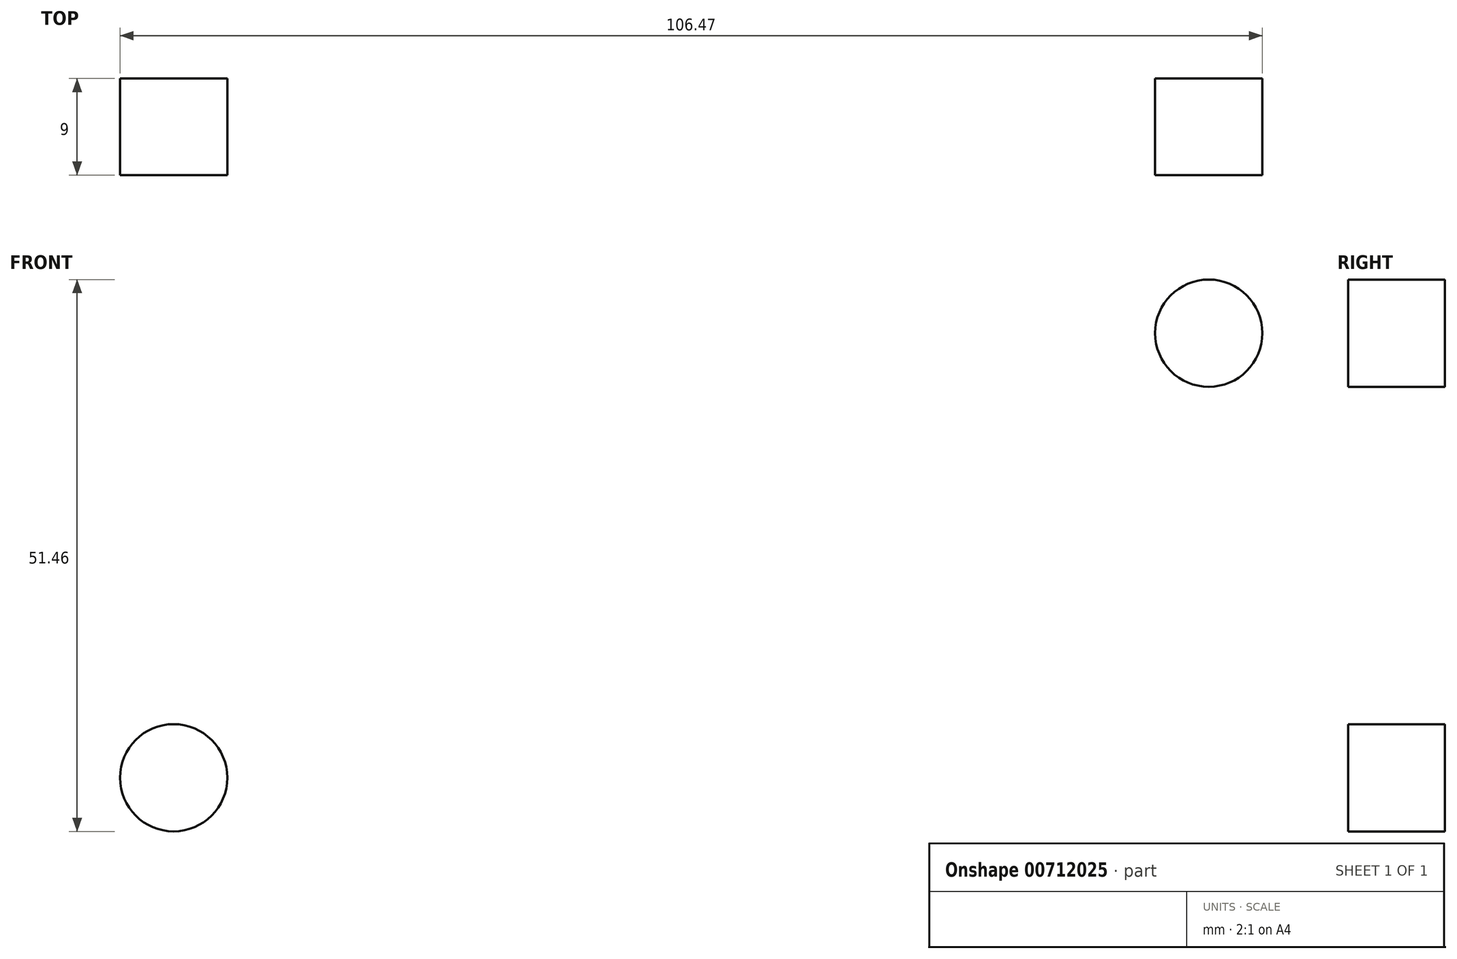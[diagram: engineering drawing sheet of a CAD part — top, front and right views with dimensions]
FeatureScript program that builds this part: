
annotation { "Feature Type Name" : "Feature", "Feature Type Description" : "" }
export const myFeature = defineFeature(function(context is Context, id is Id, definition is map)
    precondition{}
    {
        {
            var Q0;
            Q0=qCreatedBy(makeId("Front.planeOp"),FACE);
            var sketch = newSketch(context, id + "F0", { "sketchPlane" : qUnion([Q0])});
            skCircle(sketch, "E0", {"center": v(0, 0) * mm, "radius": 140 * mm});
            skArc(sketch, "E1", {"start": v(-19.84, 2.52) * mm, "mid": v(-17.32, -10) * mm, "end": v(-7.74, -18.44) * mm});
            skLineSegment(sketch, "E2", {"start": v(0, -20) * mm, "end": v(4.96, -19.38) * mm});
            skLineSegment(sketch, "E3", {"start": v(0, -20) * mm, "end": v(-4.96, -19.38) * mm});
            skArc(sketch, "E4", {"start": v(-6.37, -54.7) * mm, "mid": v(-4.56, -38.75) * mm, "end": v(-4.69, -22.7) * mm});
            skArc(sketch, "E5", {"start": v(4.69, -22.7) * mm, "mid": v(4.56, -38.75) * mm, "end": v(6.37, -54.7) * mm});
            skArc(sketch, "E6.1.0", {"start": v(50.55, 21.83) * mm, "mid": v(35.84, 15.43) * mm, "end": v(22, 7.3) * mm});
            skArc(sketch, "E6.1.1", {"start": v(17.32, 15.41) * mm, "mid": v(31.28, 23.32) * mm, "end": v(44.18, 32.86) * mm});
            skArc(sketch, "E6.2.0", {"start": v(-44.18, 32.86) * mm, "mid": v(-31.28, 23.32) * mm, "end": v(-17.32, 15.41) * mm});
            skArc(sketch, "E6.2.1", {"start": v(-22, 7.3) * mm, "mid": v(-35.84, 15.43) * mm, "end": v(-50.55, 21.83) * mm});
            skArc(sketch, "E7.trimOffspring", {"start": v(12.1, 15.93) * mm, "mid": v(0, 20) * mm, "end": v(-12.1, 15.93) * mm});
            skArc(sketch, "E8.trimOffspring", {"start": v(7.74, -18.44) * mm, "mid": v(17.32, -10) * mm, "end": v(19.84, 2.52) * mm});
            skPoint(sketch, "E9.visualSharp", {"position": v(-19.26, 5.4) * mm});
            skArc(sketch, "E9.filletArc", {"start": v(-19.84, 2.52) * mm, "mid": v(-20.25, 5.21) * mm, "end": v(-22, 7.3) * mm});
            skPoint(sketch, "E10.visualSharp", {"position": v(-14.3, 13.98) * mm});
            skArc(sketch, "E10.filletArc", {"start": v(-17.32, 15.41) * mm, "mid": v(-14.64, 14.93) * mm, "end": v(-12.1, 15.93) * mm});
            skPoint(sketch, "E11.visualSharp", {"position": v(14.3, 13.98) * mm});
            skArc(sketch, "E11.filletArc", {"start": v(12.1, 15.93) * mm, "mid": v(14.64, 14.93) * mm, "end": v(17.32, 15.41) * mm});
            skPoint(sketch, "E12.visualSharp", {"position": v(19.26, 5.4) * mm});
            skArc(sketch, "E12.filletArc", {"start": v(22, 7.3) * mm, "mid": v(20.25, 5.21) * mm, "end": v(19.84, 2.52) * mm});
            skPoint(sketch, "E13.visualSharp", {"position": v(4.96, -19.38) * mm});
            skArc(sketch, "E13.filletArc", {"start": v(7.74, -18.44) * mm, "mid": v(5.61, -20.14) * mm, "end": v(4.69, -22.7) * mm});
            skPoint(sketch, "E14.visualSharp", {"position": v(-4.96, -19.37) * mm});
            skArc(sketch, "E14.filletArc", {"start": v(-4.69, -22.7) * mm, "mid": v(-5.61, -20.14) * mm, "end": v(-7.74, -18.44) * mm});
            skCircle(sketch, "E15", {"center": v(0, 0) * mm, "radius": 3 * mm});
            skArc(sketch, "E16", {"start": v(44.7, 40.03) * mm, "mid": v(0, 60) * mm, "end": v(-44.7, 40.03) * mm});
            skArc(sketch, "E17.trimOffspring", {"start": v(-57.01, 18.7) * mm, "mid": v(-51.96, -30) * mm, "end": v(-12.32, -58.72) * mm});
            skArc(sketch, "E18.trimOffspring", {"start": v(12.32, -58.72) * mm, "mid": v(51.96, -30) * mm, "end": v(57.01, 18.7) * mm});
            skPoint(sketch, "E19.start.orphan", {"position": v(0, -52.5) * mm});
            skPoint(sketch, "E20.visualSharp", {"position": v(47.92, 36.1) * mm});
            skArc(sketch, "E20.filletArc", {"start": v(44.18, 32.86) * mm, "mid": v(45.96, 36.33) * mm, "end": v(44.7, 40.03) * mm});
            skPoint(sketch, "E21.visualSharp", {"position": v(55.23, 23.45) * mm});
            skArc(sketch, "E21.filletArc", {"start": v(57.01, 18.7) * mm, "mid": v(54.45, 21.64) * mm, "end": v(50.55, 21.83) * mm});
            skPoint(sketch, "E22.visualSharp", {"position": v(7.31, -59.55) * mm});
            skArc(sketch, "E22.filletArc", {"start": v(6.37, -54.7) * mm, "mid": v(8.49, -57.97) * mm, "end": v(12.32, -58.72) * mm});
            skPoint(sketch, "E23.visualSharp", {"position": v(-7.31, -59.55) * mm});
            skArc(sketch, "E23.filletArc", {"start": v(-12.32, -58.72) * mm, "mid": v(-8.49, -57.97) * mm, "end": v(-6.37, -54.7) * mm});
            skPoint(sketch, "E24.visualSharp", {"position": v(-55.23, 23.45) * mm});
            skArc(sketch, "E24.filletArc", {"start": v(-50.55, 21.83) * mm, "mid": v(-54.45, 21.64) * mm, "end": v(-57.01, 18.7) * mm});
            skPoint(sketch, "E25.visualSharp", {"position": v(-47.92, 36.1) * mm});
            skArc(sketch, "E25.filletArc", {"start": v(-44.7, 40.03) * mm, "mid": v(-45.96, 36.33) * mm, "end": v(-44.18, 32.86) * mm});
            skSolve(sketch);
        }
        {
            var Q0;
            Q0=makeQuery(id+"F0.imprint","IMPRINT",FACE,{"disambiguationData":[TD([[makeQuery(id+"F0.imprint","IMPRINT",EDGE,{"derivedFrom":sQuery(id+"F0.wireOp",EDGE,"E0")}),1.0]])]});
            extrude(context, id + "F1", {"entities" : qUnion([Q0]), "depth" : 9 * mm, "offsetDistance" : 25 * mm});
        }
        {
            var Q0;
            Q0=makeQuery(id+"F1.opExtrude","CAP_FACE",FACE,{"disambiguationData":[OSD([sQuery(id+"F0.wireOp",EDGE,"E0"),sQuery(id+"F0.wireOp",EDGE,"ZIODKena-zUbL-tIHl-ZjhE-ZrVelXlwY1Jm"),sQuery(id+"F0.wireOp",EDGE,"E1"),sQuery(id+"F0.wireOp",EDGE,"E4"),sQuery(id+"F0.wireOp",EDGE,"E5"),sQuery(id+"F0.wireOp",EDGE,"E6.1.0"),sQuery(id+"F0.wireOp",EDGE,"E6.1.1"),sQuery(id+"F0.wireOp",EDGE,"E6.2.0"),sQuery(id+"F0.wireOp",EDGE,"E6.2.1"),sQuery(id+"F0.wireOp",EDGE,"E7.trimOffspring"),sQuery(id+"F0.wireOp",EDGE,"76695641-9587-4a37-a800-fdab59d5437e.trimOffspring"),sQuery(id+"F0.wireOp",EDGE,"f6a8adc9-3116-4a73-b52b-f80456312e99.trimOffspring"),sQuery(id+"F0.wireOp",EDGE,"E8.trimOffspring"),sQuery(id+"F0.wireOp",EDGE,"148b025b-7aa4-4f89-82ff-914ac9d1939e.filletArc"),sQuery(id+"F0.wireOp",EDGE,"86ef975f-c508-4600-84ae-cfea6c1fc3ab.filletArc"),sQuery(id+"F0.wireOp",EDGE,"E9.filletArc"),sQuery(id+"F0.wireOp",EDGE,"E10.filletArc"),sQuery(id+"F0.wireOp",EDGE,"E11.filletArc"),sQuery(id+"F0.wireOp",EDGE,"f91f4047-f748-427d-8daf-de76601a4d34.filletArc"),sQuery(id+"F0.wireOp",EDGE,"E12.filletArc"),sQuery(id+"F0.wireOp",EDGE,"b79df10b-0bd3-4566-90f7-f9393d15810a.filletArc"),sQuery(id+"F0.wireOp",EDGE,"80464fdd-c0e1-48fa-a2d0-9debf860864b.filletArc"),sQuery(id+"F0.wireOp",EDGE,"4b7ce50a-a466-4e5d-bdfc-4ef1ba62d836.filletArc"),sQuery(id+"F0.wireOp",EDGE,"E13.filletArc"),sQuery(id+"F0.wireOp",EDGE,"E14.filletArc"),sQuery(id+"F0.wireOp",EDGE,"E15")])],"isStart":true});
            var sketch = newSketch(context, id + "F2", { "sketchPlane" : qUnion([Q0])});
            skCircle(sketch, "E26", {"center": v(0, 0) * mm, "radius": 105 * mm});
            skCircle(sketch, "E27", {"center": v(96.47, -41.46) * mm, "radius": 5 * mm});
            skCircle(sketch, "E28.1.0", {"center": v(84.14, 62.81) * mm, "radius": 5 * mm});
            skCircle(sketch, "E28.2.0", {"center": v(-12.33, 104.27) * mm, "radius": 5 * mm});
            skCircle(sketch, "E28.3.0", {"center": v(-96.47, 41.46) * mm, "radius": 5 * mm});
            skCircle(sketch, "E28.4.0", {"center": v(-84.14, -62.81) * mm, "radius": 5 * mm});
            skCircle(sketch, "E28.5.0", {"center": v(12.33, -104.27) * mm, "radius": 5 * mm});
            skSolve(sketch);
        }
        {
            var Q0;
            {var subQ0=sQuery(id+"F2.wireOp",EDGE,"E28.4.0");var subQ1=sQuery(id+"F2.wireOp",EDGE,"E26");var subQ2=makeQuery(id+"F2.imprint","INTERSECT",VERTEX,{"disambiguationData":[OD(0.0)],"derivedFrom":[subQ1,subQ0]});Q0=makeQuery(id+"F2.imprint","IMPRINT",FACE,{"disambiguationData":[TD([[makeQuery(id+"F2.imprint","IMPRINT",EDGE,{"disambiguationData":[TD([[subQ2,-1.0]])],"derivedFrom":subQ1}),-1.0]])]});}
            var Q1;
            {var subQ0=sQuery(id+"F2.wireOp",EDGE,"E28.4.0");var subQ1=sQuery(id+"F2.wireOp",EDGE,"E26");var subQ2=makeQuery(id+"F2.imprint","INTERSECT",VERTEX,{"disambiguationData":[OD(0.0)],"derivedFrom":[subQ1,subQ0]});Q1=makeQuery(id+"F2.imprint","IMPRINT",FACE,{"disambiguationData":[TD([[makeQuery(id+"F2.imprint","IMPRINT",EDGE,{"disambiguationData":[TD([[subQ2,-1.0]])],"derivedFrom":subQ1}),1.0]])]});}
            var Q2;
            {var subQ0=sQuery(id+"F2.wireOp",EDGE,"E28.3.0");var subQ1=sQuery(id+"F2.wireOp",EDGE,"E26");var subQ2=makeQuery(id+"F2.imprint","INTERSECT",VERTEX,{"disambiguationData":[OD(0.0)],"derivedFrom":[subQ1,subQ0]});Q2=makeQuery(id+"F2.imprint","IMPRINT",FACE,{"disambiguationData":[TD([[makeQuery(id+"F2.imprint","IMPRINT",EDGE,{"disambiguationData":[TD([[subQ2,-1.0]])],"derivedFrom":subQ1}),-1.0]])]});}
            var Q3;
            {var subQ0=sQuery(id+"F2.wireOp",EDGE,"E28.3.0");var subQ1=sQuery(id+"F2.wireOp",EDGE,"E26");var subQ2=makeQuery(id+"F2.imprint","INTERSECT",VERTEX,{"disambiguationData":[OD(0.0)],"derivedFrom":[subQ1,subQ0]});Q3=makeQuery(id+"F2.imprint","IMPRINT",FACE,{"disambiguationData":[TD([[makeQuery(id+"F2.imprint","IMPRINT",EDGE,{"disambiguationData":[TD([[subQ2,-1.0]])],"derivedFrom":subQ1}),1.0]])]});}
            var Q4;
            {var subQ0=sQuery(id+"F2.wireOp",EDGE,"E28.2.0");var subQ1=sQuery(id+"F2.wireOp",EDGE,"E26");var subQ2=makeQuery(id+"F2.imprint","INTERSECT",VERTEX,{"disambiguationData":[OD(0.0)],"derivedFrom":[subQ1,subQ0]});Q4=makeQuery(id+"F2.imprint","IMPRINT",FACE,{"disambiguationData":[TD([[makeQuery(id+"F2.imprint","IMPRINT",EDGE,{"disambiguationData":[TD([[subQ2,-1.0]])],"derivedFrom":subQ1}),-1.0]])]});}
            var Q5;
            {var subQ0=sQuery(id+"F2.wireOp",EDGE,"E28.2.0");var subQ1=sQuery(id+"F2.wireOp",EDGE,"E26");var subQ2=makeQuery(id+"F2.imprint","INTERSECT",VERTEX,{"disambiguationData":[OD(0.0)],"derivedFrom":[subQ1,subQ0]});Q5=makeQuery(id+"F2.imprint","IMPRINT",FACE,{"disambiguationData":[TD([[makeQuery(id+"F2.imprint","IMPRINT",EDGE,{"disambiguationData":[TD([[subQ2,-1.0]])],"derivedFrom":subQ1}),1.0]])]});}
            var Q6;
            {var subQ0=sQuery(id+"F2.wireOp",EDGE,"E28.1.0");var subQ1=sQuery(id+"F2.wireOp",EDGE,"E26");var subQ2=makeQuery(id+"F2.imprint","INTERSECT",VERTEX,{"disambiguationData":[OD(0.0)],"derivedFrom":[subQ1,subQ0]});Q6=makeQuery(id+"F2.imprint","IMPRINT",FACE,{"disambiguationData":[TD([[makeQuery(id+"F2.imprint","IMPRINT",EDGE,{"disambiguationData":[TD([[subQ2,1.0]])],"derivedFrom":subQ1}),1.0]])]});}
            var Q7;
            {var subQ0=sQuery(id+"F2.wireOp",EDGE,"E28.1.0");var subQ1=sQuery(id+"F2.wireOp",EDGE,"E26");var subQ2=makeQuery(id+"F2.imprint","INTERSECT",VERTEX,{"disambiguationData":[OD(0.0)],"derivedFrom":[subQ1,subQ0]});Q7=makeQuery(id+"F2.imprint","IMPRINT",FACE,{"disambiguationData":[TD([[makeQuery(id+"F2.imprint","IMPRINT",EDGE,{"disambiguationData":[TD([[subQ2,1.0]])],"derivedFrom":subQ1}),-1.0]])]});}
            var Q8;
            {var subQ0=sQuery(id+"F2.wireOp",EDGE,"E27");var subQ1=sQuery(id+"F2.wireOp",EDGE,"E26");var subQ2=makeQuery(id+"F2.imprint","INTERSECT",VERTEX,{"disambiguationData":[OD(0.0)],"derivedFrom":[subQ1,subQ0]});Q8=makeQuery(id+"F2.imprint","IMPRINT",FACE,{"disambiguationData":[TD([[makeQuery(id+"F2.imprint","IMPRINT",EDGE,{"disambiguationData":[TD([[subQ2,-1.0]])],"derivedFrom":subQ1}),1.0]])]});}
            var Q9;
            {var subQ0=sQuery(id+"F2.wireOp",EDGE,"E27");var subQ1=sQuery(id+"F2.wireOp",EDGE,"E26");var subQ2=makeQuery(id+"F2.imprint","INTERSECT",VERTEX,{"disambiguationData":[OD(0.0)],"derivedFrom":[subQ1,subQ0]});Q9=makeQuery(id+"F2.imprint","IMPRINT",FACE,{"disambiguationData":[TD([[makeQuery(id+"F2.imprint","IMPRINT",EDGE,{"disambiguationData":[TD([[subQ2,-1.0]])],"derivedFrom":subQ1}),-1.0]])]});}
            var Q10;
            {var subQ0=sQuery(id+"F2.wireOp",EDGE,"E28.5.0");var subQ1=sQuery(id+"F2.wireOp",EDGE,"E26");var subQ2=makeQuery(id+"F2.imprint","INTERSECT",VERTEX,{"disambiguationData":[OD(0.0)],"derivedFrom":[subQ1,subQ0]});Q10=makeQuery(id+"F2.imprint","IMPRINT",FACE,{"disambiguationData":[TD([[makeQuery(id+"F2.imprint","IMPRINT",EDGE,{"disambiguationData":[TD([[subQ2,-1.0]])],"derivedFrom":subQ1}),1.0]])]});}
            var Q11;
            {var subQ0=sQuery(id+"F2.wireOp",EDGE,"E28.5.0");var subQ1=sQuery(id+"F2.wireOp",EDGE,"E26");var subQ2=makeQuery(id+"F2.imprint","INTERSECT",VERTEX,{"disambiguationData":[OD(0.0)],"derivedFrom":[subQ1,subQ0]});Q11=makeQuery(id+"F2.imprint","IMPRINT",FACE,{"disambiguationData":[TD([[makeQuery(id+"F2.imprint","IMPRINT",EDGE,{"disambiguationData":[TD([[subQ2,-1.0]])],"derivedFrom":subQ1}),-1.0]])]});}
            extrude(context, id + "F3", {"entities" : qUnion([Q0, Q1, Q2, Q3, Q4, Q5, Q6, Q7, Q8, Q9, Q10, Q11]), "operationType" : NewBodyOperationType.REMOVE, "oppositeDirection" : true, "depth" : 25 * mm, "offsetDistance" : 25 * mm});
        }
    });
